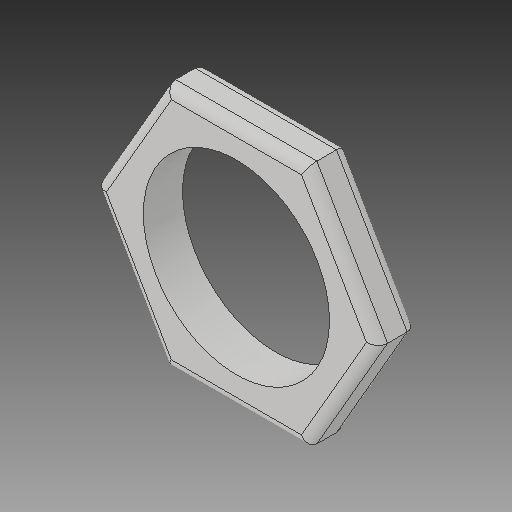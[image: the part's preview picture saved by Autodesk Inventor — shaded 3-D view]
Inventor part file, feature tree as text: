
AUTODESK INVENTOR PART (.ipt)
format: ipt  version: 2017 (Build 210142000, 142)  size: 118,272 bytes
history: native  units: in
note: dims shown in document units (in); Inventor stores cm internally (conversion verified against a paired STEP export)
features: fillet x1
ambient origin geometry x8: Origin, YZ Plane, XZ Plane, XY Plane, X Axis, Y Axis, Z Axis, Center Point
bodies: Solid1 (feature_tree)
feature tree (1):
  fillet  "Fillet1"  [1 undecoded]
note: 1 required parameter value undecoded (feature->parameter linkage not recoverable at this tier; creation-order binding heuristic only, values carry confidence <= 0.55)
